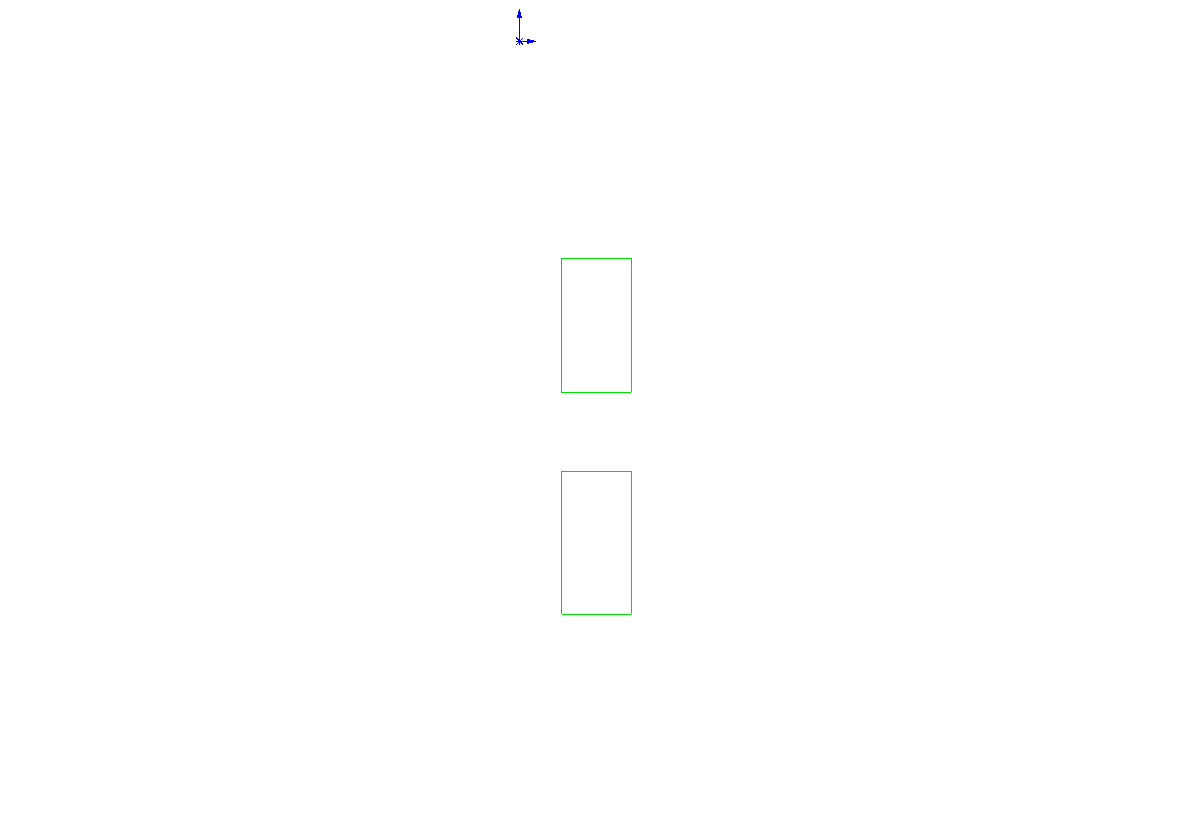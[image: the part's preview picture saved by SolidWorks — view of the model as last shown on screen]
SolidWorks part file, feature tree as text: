
SOLIDWORKS PART (.sldprt)
format: sldprt  version: not decoded by parser v0  size: 142,336 bytes
history: native  units: mm
features: sketch x4, cut_extrude x3, material x1, extrude x1 (+13 scaffold rows collapsed)
feature tree (22):
  scaffold x13  (default folders/planes/origin — collapsed)
  material  "Material <not specified>"
  sketch  "Sketch1"  dims[D1=18.542mm D2=95.25mm]
  extrude  "Extrude1"  Depth=1.6002mm
  sketch  "Sketch2"  dims[D1=3.6068mm D2=3.5052mm D3=9.525mm D4=6.35mm D5=9.525mm D6=6.35mm]
  cut_extrude  "Cut-Extrude1"  Depth=1.6002mm
  sketch  "Sketch3"  dims[D1=3.556mm D2=4.7498mm D3=11.43mm D4=5.6388mm D5=63.5mm]
  cut_extrude  "Cut-Extrude2"  Depth=2.54mm
  sketch  "Sketch4"  dims[c1.D3=3.556mm c1.D2=3.556mm c1.D7=3.556mm c1.D1=20.32mm c2.D2=8.89mm c2.D3=9.525mm c2.D4=3.175mm c2.D5=20.32mm c2.D6=9.525mm c2.D7=8.89mm c2.D8=3.175mm]
  cut_extrude  "Fiber Holes"  Depth=2.54mm
decode coverage: 8 of 8 modeling features carry decoded parameters
note: suppression state not decoded; provenance and decode notes live in map.json
